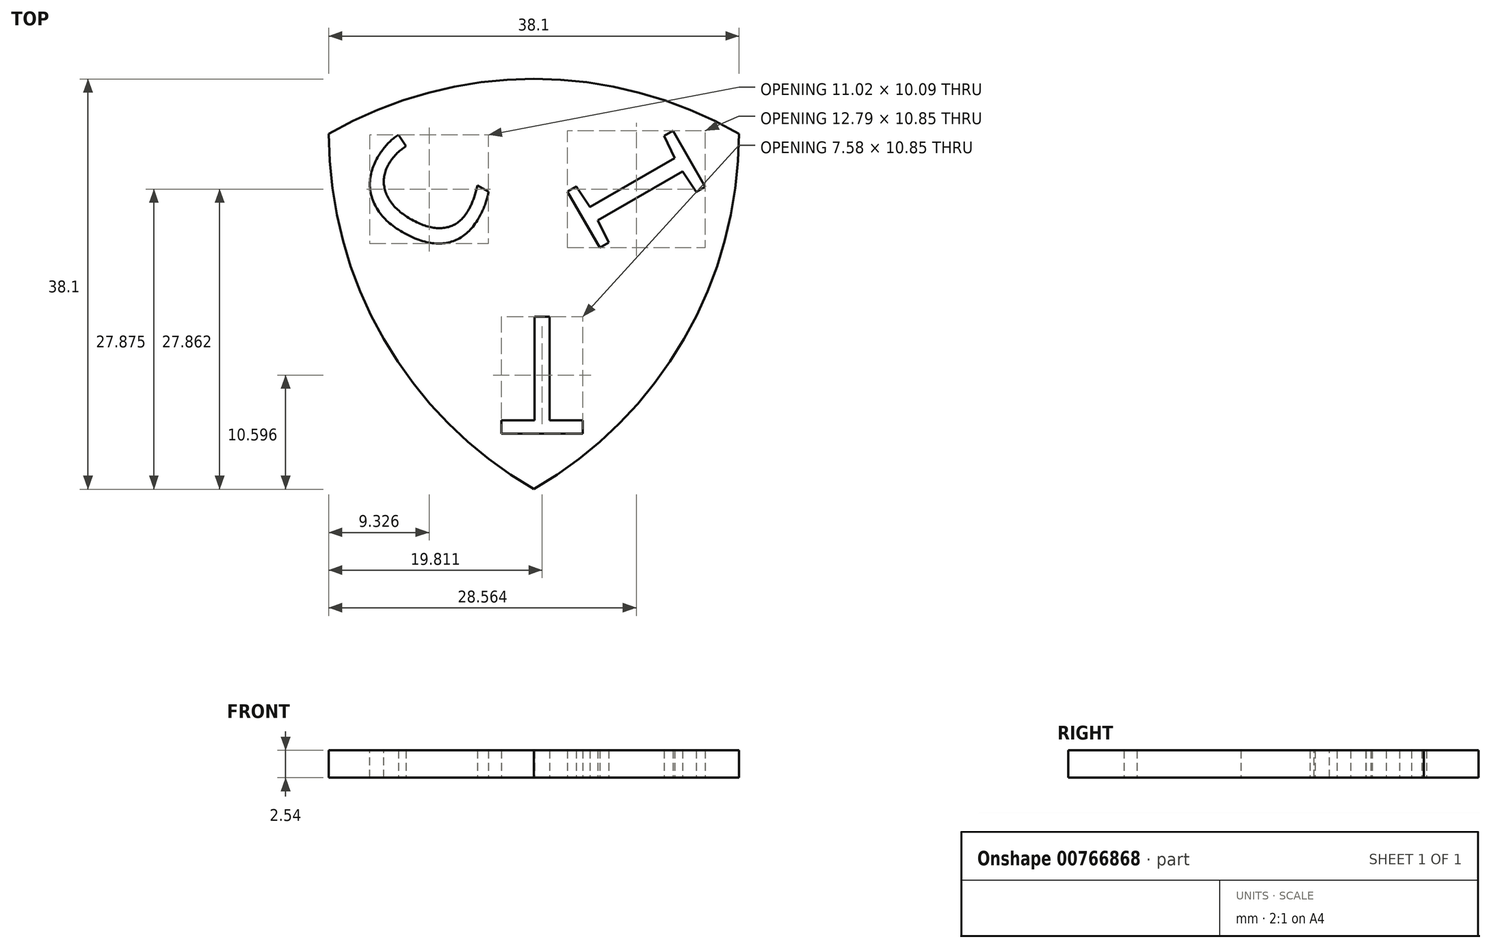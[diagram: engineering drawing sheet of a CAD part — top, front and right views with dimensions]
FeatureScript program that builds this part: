
annotation { "Feature Type Name" : "Feature", "Feature Type Description" : "" }
export const myFeature = defineFeature(function(context is Context, id is Id, definition is map)
    precondition{}
    {
        {
            var Q0;
            Q0=qCreatedBy(makeId("Top.planeOp"),FACE);
            var sketch = newSketch(context, id + "F0", { "sketchPlane" : qUnion([Q0])});
            skCircle(sketch, "E0", {"center": v(0, 0) * mm, "radius": 38.1 * mm});
            skSolve(sketch);
        }
        {
            var Q0;
            Q0=qCreatedBy(makeId("Top.planeOp"),FACE);
            var sketch = newSketch(context, id + "F1", { "sketchPlane" : qUnion([Q0])});
            skCircle(sketch, "E1", {"center": v(-38.1, 0) * mm, "radius": 38.1 * mm});
            skSolve(sketch);
        }
        {
            var Q0;
            Q0=qCreatedBy(makeId("Top.planeOp"),FACE);
            var sketch = newSketch(context, id + "F2", { "sketchPlane" : qUnion([Q0])});
            skCircle(sketch, "E2", {"center": v(-19.05, -33) * mm, "radius": 38.1 * mm});
            skSolve(sketch);
        }
        {
            var Q0;
            Q0=makeQuery(id+"F0.imprint","IMPRINT",FACE,{"disambiguationData":[TD([[makeQuery(id+"F0.imprint","IMPRINT",EDGE,{"derivedFrom":sQuery(id+"F0.wireOp",EDGE,"E0")}),1.0]])]});
            extrude(context, id + "F3", {"entities" : qUnion([Q0]), "depth" : 2.54 * mm, "offsetDistance" : 25.4 * mm});
        }
        {
            var Q0;
            Q0=makeQuery(id+"F1.imprint","IMPRINT",FACE,{"disambiguationData":[TD([[makeQuery(id+"F1.imprint","IMPRINT",EDGE,{"derivedFrom":sQuery(id+"F1.wireOp",EDGE,"E1")}),1.0]])]});
            extrude(context, id + "F4", {"entities" : qUnion([Q0]), "depth" : 2.54 * mm, "offsetDistance" : 25.4 * mm});
        }
        {
            var Q0;
            Q0=makeQuery(id+"F2.imprint","IMPRINT",FACE,{"disambiguationData":[TD([[makeQuery(id+"F2.imprint","IMPRINT",EDGE,{"derivedFrom":sQuery(id+"F2.wireOp",EDGE,"E2")}),1.0]])]});
            extrude(context, id + "F5", {"entities" : qUnion([Q0]), "depth" : 2.54 * mm, "offsetDistance" : 25.4 * mm});
        }
        {
            var Q0;
            Q0=makeQuery(id+"F4.opExtrude","SWEPT_BODY",BODY,{"disambiguationData":[OSD([sQuery(id+"F1.wireOp",EDGE,"E1")])]});
            var Q1;
            Q1=makeQuery(id+"F5.opExtrude","SWEPT_BODY",BODY,{"disambiguationData":[OSD([sQuery(id+"F2.wireOp",EDGE,"E2")])]});
            booleanBodies(context, id + "F6", {"operationType" : BooleanOperationType.INTERSECTION, "tools" : qUnion([Q0, Q1])});
        }
        {
            var Q0;
            Q0=makeQuery(id+"F6.opBoolean","INTERSECT",BODY,{"derivedFrom":[makeQuery(id+"F4.opExtrude","SWEPT_BODY",BODY,{"disambiguationData":[OSD([sQuery(id+"F1.wireOp",EDGE,"E1")])]}),makeQuery(id+"F5.opExtrude","SWEPT_BODY",BODY,{"disambiguationData":[OSD([sQuery(id+"F2.wireOp",EDGE,"E2")])]})]});
            var Q1;
            Q1=makeQuery(id+"F3.opExtrude","SWEPT_BODY",BODY,{"disambiguationData":[OSD([sQuery(id+"F0.wireOp",EDGE,"E0")])]});
            booleanBodies(context, id + "F7", {"operationType" : BooleanOperationType.INTERSECTION, "tools" : qUnion([Q0, Q1])});
        }
        {
            var Q0;
            Q0=qCreatedBy(makeId("Top.planeOp"),FACE);
            var sketch = newSketch(context, id + "F8", { "sketchPlane" : qUnion([Q0])});
            skText(sketch, "E3", { "text": "C", "fontName": "DroidSansMono.ttf"});
            skText(sketch, "E4", { "text": "I", "fontName": "DroidSansMono.ttf"});
            skText(sketch, "E5", { "text": "T", "fontName": "DroidSansMono.ttf"});
            const initialGuessF8  = {"E3": [-0.02711, -0.0126, 0.5, 0.86603, 0.01073], "E4": [-0.0168, -0.00386, 0.5, -0.86603, 0.0114], "E5": [-0.01374, -0.01698, -1, 0, 0.01094]};
            skSetInitialGuess(sketch, initialGuessF8);
            skSolve(sketch);
        }
        {
            var Q0;
            Q0 = qSketchRegion(id + "F8", true);
            extrude(context, id + "F9", {"entities" : qUnion([Q0]), "depth" : 5.08 * mm, "offsetDistance" : 25.4 * mm});
        }
        {
            var Q0;
            Q0=makeQuery(id+"F9.opExtrude","SWEPT_BODY",BODY,{"disambiguationData":[OSD([sQuery(id+"F8.wireOp",EDGE,"E3.sketch_text.stroke-0"),sQuery(id+"F8.wireOp",EDGE,"E3.sketch_text.stroke-1"),sQuery(id+"F8.wireOp",EDGE,"E3.sketch_text.stroke-2"),sQuery(id+"F8.wireOp",EDGE,"E3.sketch_text.stroke-3"),sQuery(id+"F8.wireOp",EDGE,"E3.sketch_text.stroke-4"),sQuery(id+"F8.wireOp",EDGE,"E3.sketch_text.stroke-5"),sQuery(id+"F8.wireOp",EDGE,"E3.sketch_text.stroke-6"),sQuery(id+"F8.wireOp",EDGE,"E3.sketch_text.stroke-7"),sQuery(id+"F8.wireOp",EDGE,"E3.sketch_text.stroke-8"),sQuery(id+"F8.wireOp",EDGE,"E3.sketch_text.stroke-9"),sQuery(id+"F8.wireOp",EDGE,"E3.sketch_text.stroke-10"),sQuery(id+"F8.wireOp",EDGE,"E3.sketch_text.stroke-11"),sQuery(id+"F8.wireOp",EDGE,"E3.sketch_text.stroke-12"),sQuery(id+"F8.wireOp",EDGE,"E3.sketch_text.stroke-13")])]});
            var Q1;
            Q1=makeQuery(id+"F9.opExtrude","SWEPT_BODY",BODY,{"disambiguationData":[OSD([sQuery(id+"F8.wireOp",EDGE,"E4.sketch_text.stroke-0"),sQuery(id+"F8.wireOp",EDGE,"E4.sketch_text.stroke-1"),sQuery(id+"F8.wireOp",EDGE,"E4.sketch_text.stroke-2"),sQuery(id+"F8.wireOp",EDGE,"E4.sketch_text.stroke-3"),sQuery(id+"F8.wireOp",EDGE,"E4.sketch_text.stroke-4"),sQuery(id+"F8.wireOp",EDGE,"E4.sketch_text.stroke-5"),sQuery(id+"F8.wireOp",EDGE,"E4.sketch_text.stroke-6"),sQuery(id+"F8.wireOp",EDGE,"E4.sketch_text.stroke-7"),sQuery(id+"F8.wireOp",EDGE,"E4.sketch_text.stroke-8"),sQuery(id+"F8.wireOp",EDGE,"E4.sketch_text.stroke-9"),sQuery(id+"F8.wireOp",EDGE,"E4.sketch_text.stroke-10"),sQuery(id+"F8.wireOp",EDGE,"E4.sketch_text.stroke-11")])]});
            var Q2;
            Q2=makeQuery(id+"F9.opExtrude","SWEPT_BODY",BODY,{"disambiguationData":[OSD([sQuery(id+"F8.wireOp",EDGE,"E5.sketch_text.stroke-0"),sQuery(id+"F8.wireOp",EDGE,"E5.sketch_text.stroke-1"),sQuery(id+"F8.wireOp",EDGE,"E5.sketch_text.stroke-2"),sQuery(id+"F8.wireOp",EDGE,"E5.sketch_text.stroke-3"),sQuery(id+"F8.wireOp",EDGE,"E5.sketch_text.stroke-4"),sQuery(id+"F8.wireOp",EDGE,"E5.sketch_text.stroke-5"),sQuery(id+"F8.wireOp",EDGE,"E5.sketch_text.stroke-6"),sQuery(id+"F8.wireOp",EDGE,"E5.sketch_text.stroke-7")])]});
            var Q3;
            Q3=makeQuery(id+"F7.opBoolean","INTERSECT",BODY,{"derivedFrom":[makeQuery(id+"F3.opExtrude","SWEPT_BODY",BODY,{"disambiguationData":[OSD([sQuery(id+"F0.wireOp",EDGE,"E0")])]}),makeQuery(id+"F6.opBoolean","INTERSECT",BODY,{"derivedFrom":[makeQuery(id+"F4.opExtrude","SWEPT_BODY",BODY,{"disambiguationData":[OSD([sQuery(id+"F1.wireOp",EDGE,"E1")])]}),makeQuery(id+"F5.opExtrude","SWEPT_BODY",BODY,{"disambiguationData":[OSD([sQuery(id+"F2.wireOp",EDGE,"E2")])]})]})]});
            booleanBodies(context, id + "F10", {"operationType" : BooleanOperationType.SUBTRACTION, "tools" : qUnion([Q0, Q1, Q2]), "targets" : qUnion([Q3])});
        }
    });
